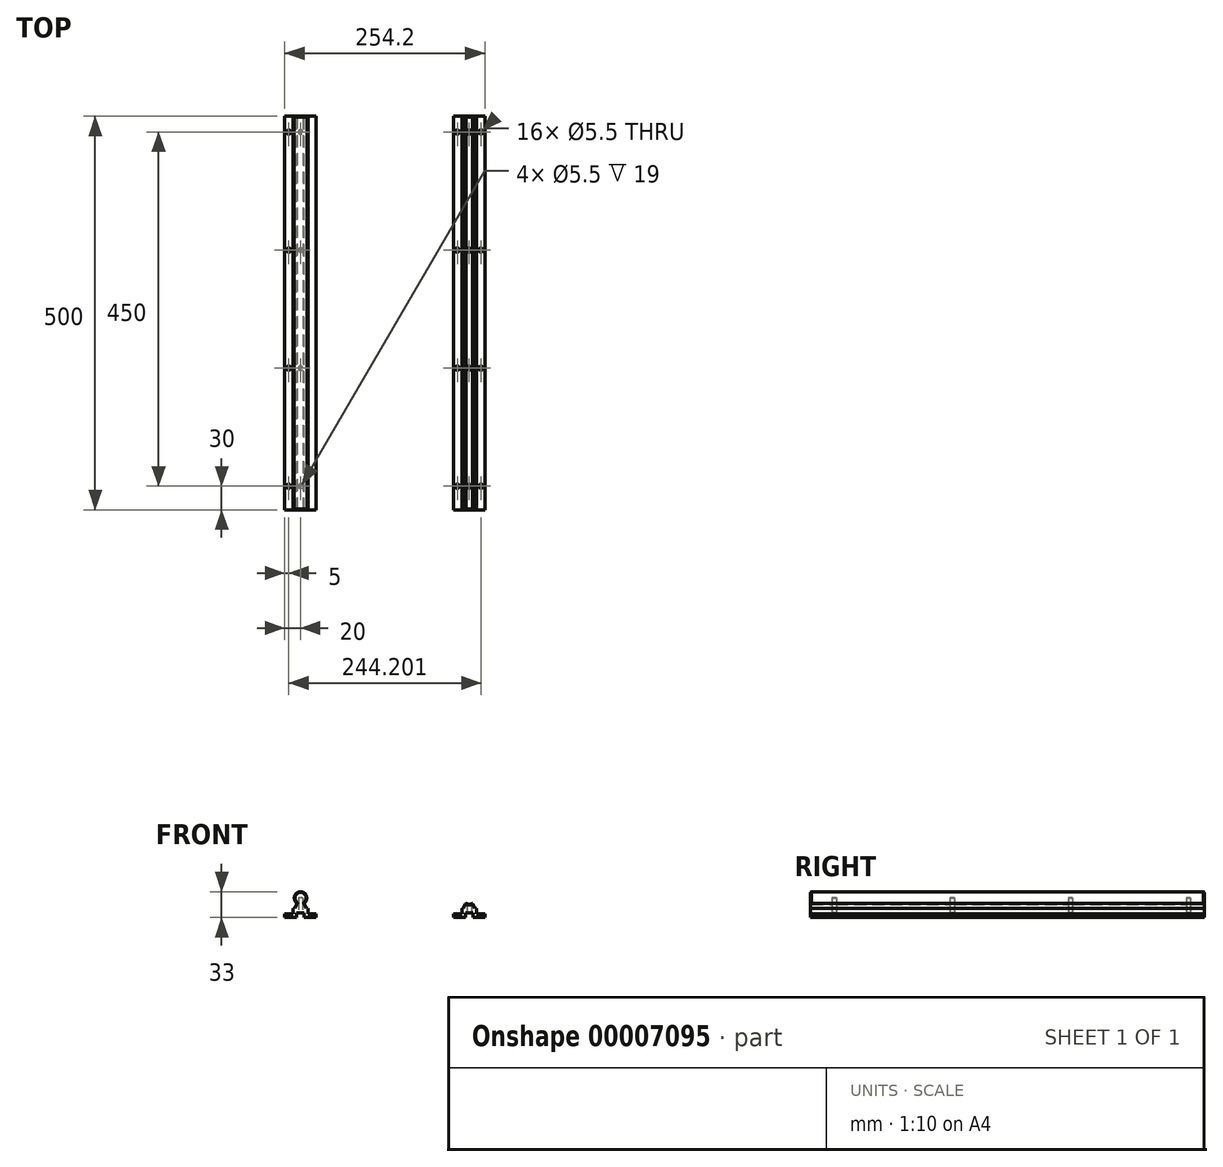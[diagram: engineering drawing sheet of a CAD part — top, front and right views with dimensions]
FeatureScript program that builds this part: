
annotation { "Feature Type Name" : "Feature", "Feature Type Description" : "" }
export const myFeature = defineFeature(function(context is Context, id is Id, definition is map)
    precondition{}
    {
        {
            var Q0;
            Q0=qCreatedBy(makeId("Front.planeOp"),FACE);
            var sketch = newSketch(context, id + "F0", { "sketchPlane" : qUnion([Q0])});
            skCircle(sketch, "E0", {"center": v(0, 25) * mm, "radius": 8 * mm});
            skLineSegment(sketch, "E1", {"start": v(-4, 18.07) * mm, "end": v(-7.68, 11.7) * mm});
            skLineSegment(sketch, "E2", {"start": v(-7.68, 11.7) * mm, "end": v(-9.25, 11.7) * mm});
            skLineSegment(sketch, "E3", {"start": v(-9.25, 11.7) * mm, "end": v(-9.25, 5) * mm});
            skLineSegment(sketch, "E4", {"start": v(-9.25, 5) * mm, "end": v(-20, 5) * mm});
            skLineSegment(sketch, "E5", {"start": v(-20, 5) * mm, "end": v(-20, 0) * mm});
            skLineSegment(sketch, "E6", {"start": v(-20, 0) * mm, "end": v(-4.75, 0) * mm});
            skLineSegment(sketch, "E7", {"start": v(-4.75, 0) * mm, "end": v(-4.75, 6) * mm});
            skLineSegment(sketch, "E8", {"start": v(-4.75, 6) * mm, "end": v(0, 6) * mm});
            skLineSegment(sketch, "E9.0.MirrorCS", {"start": v(4, 18.07) * mm, "end": v(7.68, 11.7) * mm});
            skLineSegment(sketch, "E10.0.MirrorCS", {"start": v(7.68, 11.7) * mm, "end": v(9.25, 11.7) * mm});
            skLineSegment(sketch, "E11.0.MirrorCS", {"start": v(9.25, 11.7) * mm, "end": v(9.25, 5) * mm});
            skLineSegment(sketch, "E12.0.MirrorCS", {"start": v(9.25, 5) * mm, "end": v(20, 5) * mm});
            skLineSegment(sketch, "E13.0.MirrorCS", {"start": v(20, 5) * mm, "end": v(20, 0) * mm});
            skLineSegment(sketch, "E14.0.MirrorCS", {"start": v(20, 0) * mm, "end": v(4.75, 0) * mm});
            skLineSegment(sketch, "E15.0.MirrorCS", {"start": v(4.75, 0) * mm, "end": v(4.75, 6) * mm});
            skLineSegment(sketch, "E16.0.MirrorCS", {"start": v(4.75, 6) * mm, "end": v(0, 6) * mm});
            skLineSegment(sketch, "E17", {"start": v(107.1, 61.02) * mm, "end": v(107.1, -31.88) * mm, "construction": true});
            skLineSegment(sketch, "E18.0.MirrorCS", {"start": v(209.45, 0) * mm, "end": v(209.45, 6) * mm});
            skLineSegment(sketch, "E18.1.MirrorCS", {"start": v(194.2, 5) * mm, "end": v(194.2, 0) * mm});
            skLineSegment(sketch, "E18.5.MirrorCS", {"start": v(218.95, 0) * mm, "end": v(218.95, 6) * mm});
            skLineSegment(sketch, "E18.6.MirrorCS", {"start": v(206.52, 11.7) * mm, "end": v(204.95, 11.7) * mm});
            skLineSegment(sketch, "E18.7.MirrorCS", {"start": v(223.45, 5) * mm, "end": v(234.2, 5) * mm});
            skLineSegment(sketch, "E18.8.MirrorCS", {"start": v(223.45, 11.7) * mm, "end": v(223.45, 5) * mm});
            skLineSegment(sketch, "E18.9.MirrorCS", {"start": v(218.2, 18.07) * mm, "end": v(221.88, 11.7) * mm});
            skLineSegment(sketch, "E18.10.MirrorCS", {"start": v(210.2, 18.07) * mm, "end": v(206.52, 11.7) * mm});
            skLineSegment(sketch, "E18.11.MirrorCS", {"start": v(204.95, 5) * mm, "end": v(194.2, 5) * mm});
            skLineSegment(sketch, "E18.12.MirrorCS", {"start": v(234.2, 0) * mm, "end": v(218.95, 0) * mm});
            skLineSegment(sketch, "E18.13.MirrorCS", {"start": v(204.95, 11.7) * mm, "end": v(204.95, 5) * mm});
            skLineSegment(sketch, "E18.14.MirrorCS", {"start": v(194.2, 0) * mm, "end": v(209.45, 0) * mm});
            skCircle(sketch, "E18.15.MirrorC", {"center": v(214.2, 25) * mm, "radius": 8 * mm});
            skLineSegment(sketch, "E19", {"start": v(234.2, 0) * mm, "end": v(234.2, 5) * mm});
            skLineSegment(sketch, "E20", {"start": v(209.45, 6) * mm, "end": v(218.95, 6) * mm});
            skLineSegment(sketch, "E21", {"start": v(221.88, 11.7) * mm, "end": v(223.45, 11.7) * mm});
            skSolve(sketch);
        }
        {
            var Q0;
            {var subQ0=sQuery(id+"F0.wireOp",EDGE,"E0");var subQ2=makeQuery(id+"F0.imprint","INTERSECT",VERTEX,{"derivedFrom":[subQ0,sQuery(id+"F0.wireOp",EDGE,"E1")]});Q0=makeQuery(id+"F0.imprint","IMPRINT",FACE,{"disambiguationData":[TD([[makeQuery(id+"F0.imprint","IMPRINT",EDGE,{"disambiguationData":[TD([[subQ2,-1.0]])],"derivedFrom":subQ0}),1.0]])]});}
            var Q1;
            {var subQ1=sQuery(id+"F0.wireOp",EDGE,"E1");Q1=makeQuery(id+"F0.imprint","IMPRINT",FACE,{"disambiguationData":[TD([[makeQuery(id+"F0.imprint","IMPRINT",EDGE,{"derivedFrom":subQ1}),1.0]])]});}
            extrude(context, id + "F1", {"entities" : qUnion([Q0, Q1]), "depth" : 500 * mm});
        }
        {
            var Q0;
            Q0=makeQuery(id+"F0.imprint","IMPRINT",FACE,{"disambiguationData":[TD([[makeQuery(id+"F0.imprint","IMPRINT",EDGE,{"derivedFrom":sQuery(id+"F0.wireOp",EDGE,"E18.0.MirrorCS")}),1.0]])]});
            var Q1;
            {var subQ0=sQuery(id+"F0.wireOp",EDGE,"E18.15.MirrorC");var subQ2=makeQuery(id+"F0.imprint","INTERSECT",VERTEX,{"derivedFrom":[sQuery(id+"F0.wireOp",EDGE,"E18.9.MirrorCS"),subQ0]});Q1=makeQuery(id+"F0.imprint","IMPRINT",FACE,{"disambiguationData":[TD([[makeQuery(id+"F0.imprint","IMPRINT",EDGE,{"disambiguationData":[TD([[subQ2,-1.0]])],"derivedFrom":subQ0}),-1.0]])]});}
            extrude(context, id + "F2", {"entities" : qUnion([Q0, Q1]), "depth" : 500 * mm});
        }
        {
            var Q0;
            Q0=qCreatedBy(makeId("Top.planeOp"),FACE);
            var sketch = newSketch(context, id + "F3", { "sketchPlane" : qUnion([Q0])});
            skCircle(sketch, "E22", {"center": v(-15, -20) * mm, "radius": 2.75 * mm});
            skCircle(sketch, "E23", {"center": v(0, -20) * mm, "radius": 2.75 * mm});
            skCircle(sketch, "E24.0.MirrorC", {"center": v(15, -20) * mm, "radius": 2.75 * mm});
            skLineSegment(sketch, "E25", {"start": v(-15, -20) * mm, "end": v(15, -20) * mm, "construction": true});
            skCircle(sketch, "E26.0.1.0", {"center": v(-15, -170) * mm, "radius": 2.75 * mm});
            skCircle(sketch, "E26.0.1.1", {"center": v(0, -170) * mm, "radius": 2.75 * mm});
            skCircle(sketch, "E26.0.1.2", {"center": v(15, -170) * mm, "radius": 2.75 * mm});
            skCircle(sketch, "E26.0.2.0", {"center": v(-15, -320) * mm, "radius": 2.75 * mm});
            skCircle(sketch, "E26.0.2.1", {"center": v(0, -320) * mm, "radius": 2.75 * mm});
            skCircle(sketch, "E26.0.2.2", {"center": v(15, -320) * mm, "radius": 2.75 * mm});
            skCircle(sketch, "E26.0.3.0", {"center": v(-15, -470) * mm, "radius": 2.75 * mm});
            skCircle(sketch, "E26.0.3.1", {"center": v(0, -470) * mm, "radius": 2.75 * mm});
            skCircle(sketch, "E26.0.3.2", {"center": v(15, -470) * mm, "radius": 2.75 * mm});
            skCircle(sketch, "E26.0.4.0", {"center": v(-15, -620) * mm, "radius": 2.75 * mm});
            skCircle(sketch, "E26.0.4.1", {"center": v(0, -620) * mm, "radius": 2.75 * mm});
            skCircle(sketch, "E26.0.4.2", {"center": v(15, -620) * mm, "radius": 2.75 * mm});
            skCircle(sketch, "E26.0.5.0", {"center": v(-15, -770) * mm, "radius": 2.75 * mm});
            skCircle(sketch, "E26.0.5.1", {"center": v(0, -770) * mm, "radius": 2.75 * mm});
            skCircle(sketch, "E26.0.5.2", {"center": v(15, -770) * mm, "radius": 2.75 * mm});
            skCircle(sketch, "E26.0.6.0", {"center": v(-15, -920) * mm, "radius": 2.75 * mm});
            skCircle(sketch, "E26.0.6.1", {"center": v(0, -920) * mm, "radius": 2.75 * mm});
            skCircle(sketch, "E26.0.6.2", {"center": v(15, -920) * mm, "radius": 2.75 * mm});
            skLineSegment(sketch, "E26.direction1", {"start": v(-15, -20) * mm, "end": v(10, -20) * mm, "construction": true});
            skLineSegment(sketch, "E26.direction2", {"start": v(-15, -20) * mm, "end": v(-15, -170) * mm, "construction": true});
            skLineSegment(sketch, "E27", {"start": v(194.2, -20) * mm, "end": v(199.2, -20) * mm, "construction": true});
            skPoint(sketch, "E28", {"position": v(214.2, -20) * mm});
            skCircle(sketch, "E29", {"center": v(214.2, -20) * mm, "radius": 2.75 * mm});
            skCircle(sketch, "E30", {"center": v(229.2, -20) * mm, "radius": 2.75 * mm});
            skCircle(sketch, "E31", {"center": v(199.2, -20) * mm, "radius": 2.75 * mm});
            skLineSegment(sketch, "E32", {"start": v(199.2, -20) * mm, "end": v(229.2, -20) * mm, "construction": true});
            skLineSegment(sketch, "E33", {"start": v(229.2, -20) * mm, "end": v(234.2, -20) * mm, "construction": true});
            skCircle(sketch, "E34.0.1.0", {"center": v(199.2, -170) * mm, "radius": 2.75 * mm});
            skCircle(sketch, "E34.0.1.1", {"center": v(214.2, -170) * mm, "radius": 2.75 * mm});
            skCircle(sketch, "E34.0.1.2", {"center": v(229.2, -170) * mm, "radius": 2.75 * mm});
            skCircle(sketch, "E34.0.2.0", {"center": v(199.2, -320) * mm, "radius": 2.75 * mm});
            skCircle(sketch, "E34.0.2.1", {"center": v(214.2, -320) * mm, "radius": 2.75 * mm});
            skCircle(sketch, "E34.0.2.2", {"center": v(229.2, -320) * mm, "radius": 2.75 * mm});
            skCircle(sketch, "E34.0.3.0", {"center": v(199.2, -470) * mm, "radius": 2.75 * mm});
            skCircle(sketch, "E34.0.3.1", {"center": v(214.2, -470) * mm, "radius": 2.75 * mm});
            skCircle(sketch, "E34.0.3.2", {"center": v(229.2, -470) * mm, "radius": 2.75 * mm});
            skLineSegment(sketch, "E34.direction1", {"start": v(199.2, -20) * mm, "end": v(224.2, -20) * mm, "construction": true});
            skLineSegment(sketch, "E34.direction2", {"start": v(199.2, -20) * mm, "end": v(199.2, -170) * mm, "construction": true});
            skSolve(sketch);
        }
        {
            var Q0;
            {Q0=qUnion([makeQuery(id+"F3.imprint","IMPRINT",FACE,{"disambiguationData":[TD([[makeQuery(id+"F3.imprint","IMPRINT",EDGE,{"derivedFrom":sQuery(id+"F3.wireOp",EDGE,"E22")}),1.0]])]}),makeQuery(id+"F3.imprint","IMPRINT",FACE,{"disambiguationData":[TD([[makeQuery(id+"F3.imprint","IMPRINT",EDGE,{"derivedFrom":sQuery(id+"F3.wireOp",EDGE,"E23")}),1.0]])]}),makeQuery(id+"F3.imprint","IMPRINT",FACE,{"disambiguationData":[TD([[makeQuery(id+"F3.imprint","IMPRINT",EDGE,{"derivedFrom":sQuery(id+"F3.wireOp",EDGE,"E24.0.MirrorC")}),-1.0]])]}),makeQuery(id+"F3.imprint","IMPRINT",FACE,{"disambiguationData":[TD([[makeQuery(id+"F3.imprint","IMPRINT",EDGE,{"derivedFrom":sQuery(id+"F3.wireOp",EDGE,"E26.0.1.0")}),1.0]])]}),makeQuery(id+"F3.imprint","IMPRINT",FACE,{"disambiguationData":[TD([[makeQuery(id+"F3.imprint","IMPRINT",EDGE,{"derivedFrom":sQuery(id+"F3.wireOp",EDGE,"E26.0.1.1")}),1.0]])]}),makeQuery(id+"F3.imprint","IMPRINT",FACE,{"disambiguationData":[TD([[makeQuery(id+"F3.imprint","IMPRINT",EDGE,{"derivedFrom":sQuery(id+"F3.wireOp",EDGE,"E26.0.1.2")}),-1.0]])]}),makeQuery(id+"F3.imprint","IMPRINT",FACE,{"disambiguationData":[TD([[makeQuery(id+"F3.imprint","IMPRINT",EDGE,{"derivedFrom":sQuery(id+"F3.wireOp",EDGE,"E26.0.2.0")}),1.0]])]}),makeQuery(id+"F3.imprint","IMPRINT",FACE,{"disambiguationData":[TD([[makeQuery(id+"F3.imprint","IMPRINT",EDGE,{"derivedFrom":sQuery(id+"F3.wireOp",EDGE,"E26.0.2.1")}),1.0]])]}),makeQuery(id+"F3.imprint","IMPRINT",FACE,{"disambiguationData":[TD([[makeQuery(id+"F3.imprint","IMPRINT",EDGE,{"derivedFrom":sQuery(id+"F3.wireOp",EDGE,"E26.0.2.2")}),-1.0]])]}),makeQuery(id+"F3.imprint","IMPRINT",FACE,{"disambiguationData":[TD([[makeQuery(id+"F3.imprint","IMPRINT",EDGE,{"derivedFrom":sQuery(id+"F3.wireOp",EDGE,"E26.0.3.0")}),1.0]])]}),makeQuery(id+"F3.imprint","IMPRINT",FACE,{"disambiguationData":[TD([[makeQuery(id+"F3.imprint","IMPRINT",EDGE,{"derivedFrom":sQuery(id+"F3.wireOp",EDGE,"E26.0.3.1")}),1.0]])]}),makeQuery(id+"F3.imprint","IMPRINT",FACE,{"disambiguationData":[TD([[makeQuery(id+"F3.imprint","IMPRINT",EDGE,{"derivedFrom":sQuery(id+"F3.wireOp",EDGE,"E26.0.3.2")}),-1.0]])]}),makeQuery(id+"F3.imprint","IMPRINT",FACE,{"disambiguationData":[TD([[makeQuery(id+"F3.imprint","IMPRINT",EDGE,{"derivedFrom":sQuery(id+"F3.wireOp",EDGE,"E26.0.4.0")}),1.0]])]}),makeQuery(id+"F3.imprint","IMPRINT",FACE,{"disambiguationData":[TD([[makeQuery(id+"F3.imprint","IMPRINT",EDGE,{"derivedFrom":sQuery(id+"F3.wireOp",EDGE,"E26.0.4.1")}),1.0]])]}),makeQuery(id+"F3.imprint","IMPRINT",FACE,{"disambiguationData":[TD([[makeQuery(id+"F3.imprint","IMPRINT",EDGE,{"derivedFrom":sQuery(id+"F3.wireOp",EDGE,"E26.0.4.2")}),-1.0]])]}),makeQuery(id+"F3.imprint","IMPRINT",FACE,{"disambiguationData":[TD([[makeQuery(id+"F3.imprint","IMPRINT",EDGE,{"derivedFrom":sQuery(id+"F3.wireOp",EDGE,"E26.0.5.0")}),1.0]])]}),makeQuery(id+"F3.imprint","IMPRINT",FACE,{"disambiguationData":[TD([[makeQuery(id+"F3.imprint","IMPRINT",EDGE,{"derivedFrom":sQuery(id+"F3.wireOp",EDGE,"E26.0.5.1")}),1.0]])]}),makeQuery(id+"F3.imprint","IMPRINT",FACE,{"disambiguationData":[TD([[makeQuery(id+"F3.imprint","IMPRINT",EDGE,{"derivedFrom":sQuery(id+"F3.wireOp",EDGE,"E26.0.5.2")}),-1.0]])]}),makeQuery(id+"F3.imprint","IMPRINT",FACE,{"disambiguationData":[TD([[makeQuery(id+"F3.imprint","IMPRINT",EDGE,{"derivedFrom":sQuery(id+"F3.wireOp",EDGE,"E26.0.6.0")}),1.0]])]}),makeQuery(id+"F3.imprint","IMPRINT",FACE,{"disambiguationData":[TD([[makeQuery(id+"F3.imprint","IMPRINT",EDGE,{"derivedFrom":sQuery(id+"F3.wireOp",EDGE,"E26.0.6.1")}),1.0]])]}),makeQuery(id+"F3.imprint","IMPRINT",FACE,{"disambiguationData":[TD([[makeQuery(id+"F3.imprint","IMPRINT",EDGE,{"derivedFrom":sQuery(id+"F3.wireOp",EDGE,"E26.0.6.2")}),-1.0]])]}),makeQuery(id+"F3.imprint","IMPRINT",FACE,{"disambiguationData":[TD([[makeQuery(id+"F3.imprint","IMPRINT",EDGE,{"derivedFrom":sQuery(id+"F3.wireOp",EDGE,"E29")}),1.0]])]}),makeQuery(id+"F3.imprint","IMPRINT",FACE,{"disambiguationData":[TD([[makeQuery(id+"F3.imprint","IMPRINT",EDGE,{"derivedFrom":sQuery(id+"F3.wireOp",EDGE,"E30")}),1.0]])]}),makeQuery(id+"F3.imprint","IMPRINT",FACE,{"disambiguationData":[TD([[makeQuery(id+"F3.imprint","IMPRINT",EDGE,{"derivedFrom":sQuery(id+"F3.wireOp",EDGE,"E31")}),1.0]])]}),makeQuery(id+"F3.imprint","IMPRINT",FACE,{"disambiguationData":[TD([[makeQuery(id+"F3.imprint","IMPRINT",EDGE,{"derivedFrom":sQuery(id+"F3.wireOp",EDGE,"E34.0.1.0")}),1.0]])]}),makeQuery(id+"F3.imprint","IMPRINT",FACE,{"disambiguationData":[TD([[makeQuery(id+"F3.imprint","IMPRINT",EDGE,{"derivedFrom":sQuery(id+"F3.wireOp",EDGE,"E34.0.1.1")}),1.0]])]}),makeQuery(id+"F3.imprint","IMPRINT",FACE,{"disambiguationData":[TD([[makeQuery(id+"F3.imprint","IMPRINT",EDGE,{"derivedFrom":sQuery(id+"F3.wireOp",EDGE,"E34.0.1.2")}),1.0]])]}),makeQuery(id+"F3.imprint","IMPRINT",FACE,{"disambiguationData":[TD([[makeQuery(id+"F3.imprint","IMPRINT",EDGE,{"derivedFrom":sQuery(id+"F3.wireOp",EDGE,"E34.0.2.0")}),1.0]])]}),makeQuery(id+"F3.imprint","IMPRINT",FACE,{"disambiguationData":[TD([[makeQuery(id+"F3.imprint","IMPRINT",EDGE,{"derivedFrom":sQuery(id+"F3.wireOp",EDGE,"E34.0.2.1")}),1.0]])]}),makeQuery(id+"F3.imprint","IMPRINT",FACE,{"disambiguationData":[TD([[makeQuery(id+"F3.imprint","IMPRINT",EDGE,{"derivedFrom":sQuery(id+"F3.wireOp",EDGE,"E34.0.2.2")}),1.0]])]}),makeQuery(id+"F3.imprint","IMPRINT",FACE,{"disambiguationData":[TD([[makeQuery(id+"F3.imprint","IMPRINT",EDGE,{"derivedFrom":sQuery(id+"F3.wireOp",EDGE,"E34.0.3.0")}),1.0]])]}),makeQuery(id+"F3.imprint","IMPRINT",FACE,{"disambiguationData":[TD([[makeQuery(id+"F3.imprint","IMPRINT",EDGE,{"derivedFrom":sQuery(id+"F3.wireOp",EDGE,"E34.0.3.1")}),1.0]])]}),makeQuery(id+"F3.imprint","IMPRINT",FACE,{"disambiguationData":[TD([[makeQuery(id+"F3.imprint","IMPRINT",EDGE,{"derivedFrom":sQuery(id+"F3.wireOp",EDGE,"E34.0.3.2")}),1.0]])]})]);}
            extrude(context, id + "F4", {"entities" : qUnion([Q0]), "operationType" : NewBodyOperationType.REMOVE, "depth" : 25 * mm});
        }
        {
            var Q0;
            Q0=makeQuery(id+"F1.opExtrude","CAP_EDGE",EDGE,{"disambiguationData":[OSD([sQuery(id+"F0.wireOp",EDGE,"E0")])],"isStart":true});
            var Q1;
            Q1=makeQuery(id+"F1.opExtrude","CAP_EDGE",EDGE,{"disambiguationData":[OSD([sQuery(id+"F0.wireOp",EDGE,"E0")])],"isStart":false});
            var Q2;
            Q2=makeQuery(id+"F2.opExtrude","CAP_EDGE",EDGE,{"disambiguationData":[OSD([sQuery(id+"F0.wireOp",EDGE,"E18.15.MirrorC")])],"isStart":false});
            var Q3;
            Q3=makeQuery(id+"F2.opExtrude","CAP_EDGE",EDGE,{"disambiguationData":[OSD([sQuery(id+"F0.wireOp",EDGE,"E18.15.MirrorC")])],"isStart":true});
            chamfer(context, id + "F5", {"entities" : qUnion([Q0, Q1, Q2, Q3]), "width" : 1 * mm});
        }
    });
